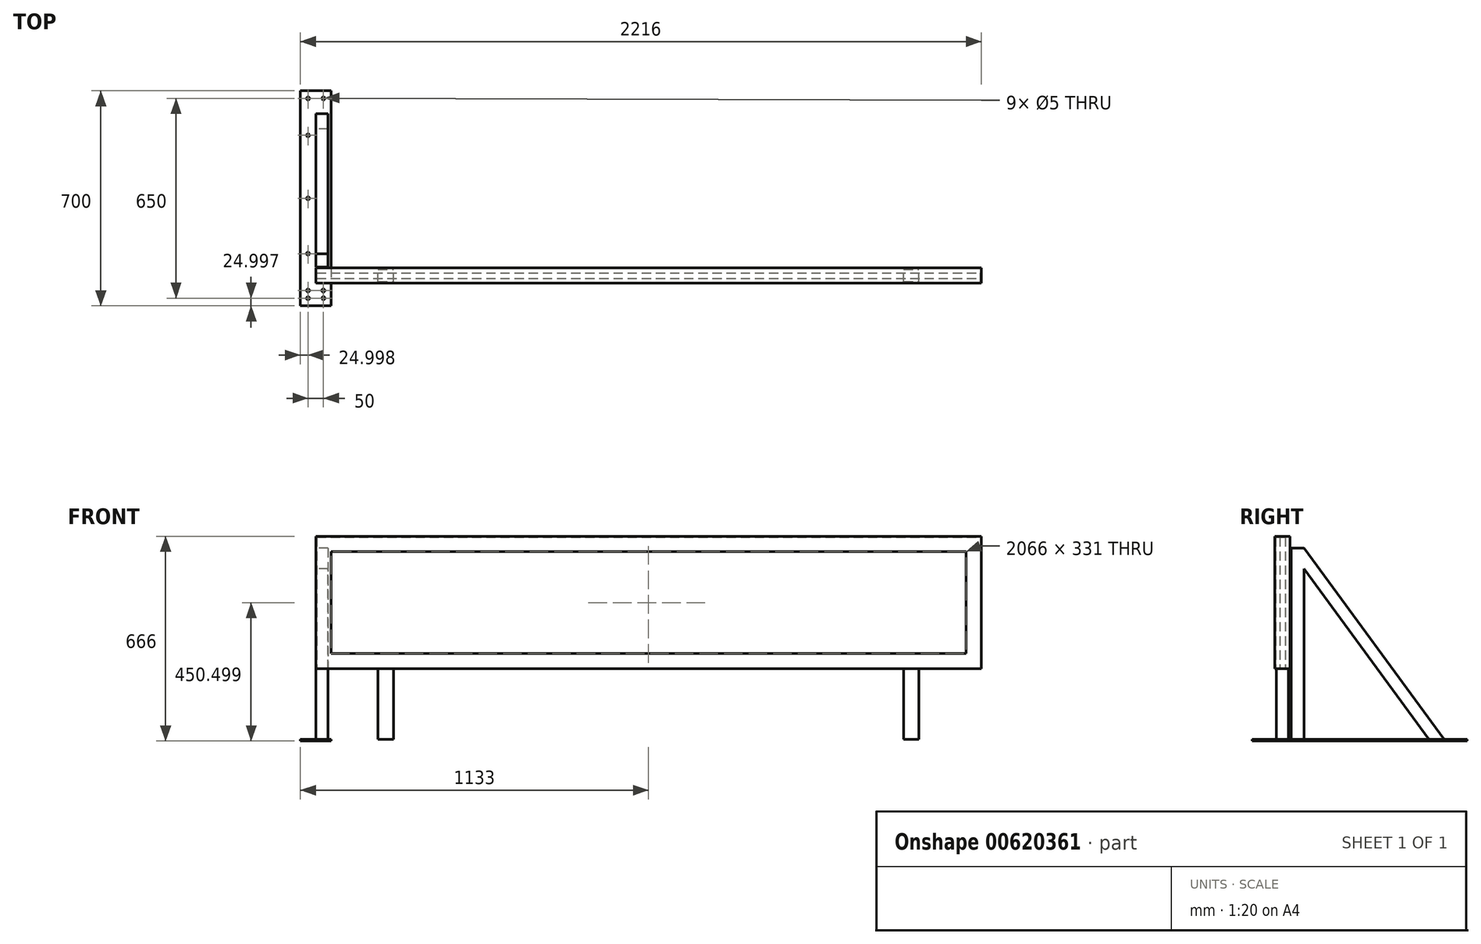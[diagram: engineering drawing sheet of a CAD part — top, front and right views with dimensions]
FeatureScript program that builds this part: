
annotation { "Feature Type Name" : "Feature", "Feature Type Description" : "" }
export const myFeature = defineFeature(function(context is Context, id is Id, definition is map)
    precondition{}
    {
        {
            var Q0;
            Q0=qCreatedBy(makeId("Front.planeOp"),FACE);
            var sketch = newSketch(context, id + "F0", { "sketchPlane" : qUnion([Q0])});
            skLineSegment(sketch, "E0.bottom", {"start": v(-2092.6, 413.56) * mm, "end": v(67.4, 413.56) * mm});
            skLineSegment(sketch, "E0.top", {"start": v(-2092.6, -11.44) * mm, "end": v(67.4, -11.44) * mm});
            skLineSegment(sketch, "E0.left", {"start": v(-2092.6, 413.56) * mm, "end": v(-2092.6, -11.44) * mm});
            skLineSegment(sketch, "E0.right", {"start": v(67.4, 413.56) * mm, "end": v(67.4, -11.44) * mm});
            skLineSegment(sketch, "E1.0", {"start": v(-2042.6, 363.56) * mm, "end": v(17.4, 363.56) * mm});
            skLineSegment(sketch, "E1.1", {"start": v(-2042.6, 363.56) * mm, "end": v(-2042.6, 38.56) * mm});
            skLineSegment(sketch, "E1.2", {"start": v(-2042.6, 38.56) * mm, "end": v(17.4, 38.56) * mm});
            skLineSegment(sketch, "E1.3", {"start": v(17.4, 363.56) * mm, "end": v(17.4, 38.56) * mm});
            skLineSegment(sketch, "E2.bottom", {"start": v(-1892.6, -11.44) * mm, "end": v(-1842.6, -11.44) * mm});
            skLineSegment(sketch, "E2.top", {"start": v(-1892.6, -244.44) * mm, "end": v(-1842.6, -244.44) * mm});
            skLineSegment(sketch, "E2.left", {"start": v(-1892.6, -14.44) * mm, "end": v(-1892.6, -244.44) * mm});
            skLineSegment(sketch, "E2.right", {"start": v(-1842.6, -14.44) * mm, "end": v(-1842.6, -244.44) * mm});
            skLineSegment(sketch, "E3.bottom", {"start": v(-182.6, -11.44) * mm, "end": v(-132.6, -11.44) * mm});
            skLineSegment(sketch, "E3.top", {"start": v(-182.6, -244.44) * mm, "end": v(-132.6, -244.44) * mm});
            skLineSegment(sketch, "E3.left", {"start": v(-182.6, -14.44) * mm, "end": v(-182.6, -244.44) * mm});
            skLineSegment(sketch, "E3.right", {"start": v(-132.6, -14.44) * mm, "end": v(-132.6, -244.44) * mm});
            skLineSegment(sketch, "E4.0", {"start": v(-2095.6, 416.56) * mm, "end": v(70.4, 416.56) * mm});
            skLineSegment(sketch, "E4.1", {"start": v(-2095.6, 416.56) * mm, "end": v(-2095.6, -14.44) * mm});
            skLineSegment(sketch, "E4.2", {"start": v(-2095.6, -14.44) * mm, "end": v(70.4, -14.44) * mm});
            skLineSegment(sketch, "E4.3", {"start": v(70.4, 416.56) * mm, "end": v(70.4, -14.44) * mm});
            skSolve(sketch);
        }
        {
            var Q0;
            Q0=makeQuery(id+"F0.imprint","IMPRINT",FACE,{"disambiguationData":[TD([[makeQuery(id+"F0.imprint","IMPRINT",EDGE,{"derivedFrom":sQuery(id+"F0.wireOp",EDGE,"E1.0")}),-1.0]])]});
            var Q1;
            Q1=makeQuery(id+"F0.imprint","IMPRINT",FACE,{"disambiguationData":[TD([[makeQuery(id+"F0.imprint","IMPRINT",EDGE,{"derivedFrom":sQuery(id+"F0.wireOp",EDGE,"E0.bottom")}),-1.0]])]});
            extrude(context, id + "F1", {"entities" : qUnion([Q0, Q1]), "endBound" : BoundingType.SYMMETRIC, "depth" : 18 * mm, "offsetDistance" : 25 * mm});
        }
        {
            var Q0;
            Q0=makeQuery(id+"F0.imprint","IMPRINT",FACE,{"disambiguationData":[TD([[makeQuery(id+"F0.imprint","IMPRINT",EDGE,{"derivedFrom":sQuery(id+"F0.wireOp",EDGE,"E0.bottom")}),1.0]])]});
            extrude(context, id + "F2", {"entities" : qUnion([Q0]), "endBound" : BoundingType.SYMMETRIC, "depth" : 50 * mm, "offsetDistance" : 25 * mm});
        }
        {
            var Q0;
            Q0=makeQuery(id+"F0.imprint","IMPRINT",FACE,{"disambiguationData":[TD([[makeQuery(id+"F0.imprint","IMPRINT",EDGE,{"derivedFrom":sQuery(id+"F0.wireOp",EDGE,"E2.top")}),1.0]])]});
            var Q1;
            Q1=makeQuery(id+"F0.imprint","IMPRINT",FACE,{"disambiguationData":[TD([[makeQuery(id+"F0.imprint","IMPRINT",EDGE,{"derivedFrom":sQuery(id+"F0.wireOp",EDGE,"E3.top")}),1.0]])]});
            extrude(context, id + "F3", {"entities" : qUnion([Q0, Q1]), "endBound" : BoundingType.SYMMETRIC, "depth" : 40 * mm, "offsetDistance" : 25 * mm});
        }
        {
            var Q0;
            Q0=makeQuery(id+"F2.opExtrude","CAP_FACE",FACE,{"disambiguationData":[OSD([sQuery(id+"F0.wireOp",EDGE,"E0.bottom"),sQuery(id+"F0.wireOp",EDGE,"E0.top"),sQuery(id+"F0.wireOp",EDGE,"E0.left"),sQuery(id+"F0.wireOp",EDGE,"E0.right"),sQuery(id+"F0.wireOp",EDGE,"E2.bottom"),sQuery(id+"F0.wireOp",EDGE,"E3.bottom"),sQuery(id+"F0.wireOp",EDGE,"E4.0"),sQuery(id+"F0.wireOp",EDGE,"E4.1"),sQuery(id+"F0.wireOp",EDGE,"E4.2"),sQuery(id+"F0.wireOp",EDGE,"E4.3")])],"isStart":false});
            var sketch = newSketch(context, id + "F4", { "sketchPlane" : qUnion([Q0])});
            skLineSegment(sketch, "E5.bottom", {"start": v(-2092.6, -11.44) * mm, "end": v(67.4, -11.44) * mm});
            skLineSegment(sketch, "E5.top", {"start": v(-2092.6, 413.56) * mm, "end": v(67.4, 413.56) * mm});
            skLineSegment(sketch, "E5.left", {"start": v(-2092.6, -11.44) * mm, "end": v(-2092.6, 413.56) * mm});
            skLineSegment(sketch, "E5.right", {"start": v(67.4, -11.44) * mm, "end": v(67.4, 413.56) * mm});
            skLineSegment(sketch, "E6.0", {"start": v(-2045.6, 35.56) * mm, "end": v(-2045.6, 366.56) * mm});
            skLineSegment(sketch, "E6.1", {"start": v(-2045.6, 35.56) * mm, "end": v(20.4, 35.56) * mm});
            skLineSegment(sketch, "E6.2", {"start": v(20.4, 35.56) * mm, "end": v(20.4, 366.56) * mm});
            skLineSegment(sketch, "E6.3", {"start": v(-2045.6, 366.56) * mm, "end": v(20.4, 366.56) * mm});
            skSolve(sketch);
        }
        {
            var Q0;
            Q0=makeQuery(id+"F4.imprint","IMPRINT",FACE,{"disambiguationData":[TD([[makeQuery(id+"F4.imprint","IMPRINT",EDGE,{"derivedFrom":sQuery(id+"F4.wireOp",EDGE,"E5.bottom")}),1.0]])]});
            extrude(context, id + "F5", {"entities" : qUnion([Q0]), "operationType" : NewBodyOperationType.ADD, "oppositeDirection" : true, "depth" : 3 * mm, "offsetDistance" : 25 * mm});
        }
        {
            var Q0;
            Q0=makeQuery(id+"F2.opExtrude","SWEPT_FACE",FACE,{"disambiguationData":[OSD([sQuery(id+"F0.wireOp",EDGE,"E4.1")])]});
            var sketch = newSketch(context, id + "F6", { "sketchPlane" : qUnion([Q0])});
            skLineSegment(sketch, "E7", {"start": v(-70.43, 310.78) * mm, "end": v(-70.43, 378.51) * mm});
            skLineSegment(sketch, "E8", {"start": v(-70.43, 378.51) * mm, "end": v(-526.28, -244.44) * mm});
            skLineSegment(sketch, "E9", {"start": v(-526.28, -244.44) * mm, "end": v(-476.71, -244.44) * mm});
            skLineSegment(sketch, "E10", {"start": v(-476.71, -244.44) * mm, "end": v(-70.43, 310.78) * mm});
            skLineSegment(sketch, "E11.bottom", {"start": v(-70.43, 378.51) * mm, "end": v(-28.18, 378.51) * mm});
            skLineSegment(sketch, "E11.top", {"start": v(-70.43, -244.44) * mm, "end": v(-28.18, -244.44) * mm});
            skLineSegment(sketch, "E11.left", {"start": v(-70.43, 378.51) * mm, "end": v(-70.43, -244.44) * mm});
            skLineSegment(sketch, "E11.right", {"start": v(-28.18, 378.51) * mm, "end": v(-28.18, -244.44) * mm});
            skLineSegment(sketch, "E12.bottom", {"start": v(-601.35, -244.44) * mm, "end": v(98.65, -244.44) * mm});
            skLineSegment(sketch, "E12.top", {"start": v(-601.35, -249.44) * mm, "end": v(98.65, -249.44) * mm});
            skLineSegment(sketch, "E12.left", {"start": v(-601.35, -244.44) * mm, "end": v(-601.35, -249.44) * mm});
            skLineSegment(sketch, "E12.right", {"start": v(98.65, -244.44) * mm, "end": v(98.65, -249.44) * mm});
            skSolve(sketch);
        }
        {
            var Q0;
            {var subQ0=sQuery(id+"F6.wireOp",EDGE,"E8");Q0=makeQuery(id+"F6.imprint","IMPRINT",FACE,{"disambiguationData":[TD([[makeQuery(id+"F6.imprint","IMPRINT",EDGE,{"derivedFrom":subQ0}),1.0]])]});}
            var Q1;
            {var subQ5=sQuery(id+"F6.wireOp",EDGE,"E11.bottom");Q1=makeQuery(id+"F6.imprint","IMPRINT",FACE,{"disambiguationData":[TD([[makeQuery(id+"F6.imprint","IMPRINT",EDGE,{"derivedFrom":subQ5}),-1.0]])]});}
            extrude(context, id + "F7", {"entities" : qUnion([Q0, Q1]), "oppositeDirection" : true, "depth" : 40 * mm, "offsetDistance" : 25 * mm});
        }
        {
            var Q0;
            Q0=makeQuery(id+"F6.imprint","IMPRINT",FACE,{"disambiguationData":[TD([[makeQuery(id+"F6.imprint","IMPRINT",EDGE,{"derivedFrom":sQuery(id+"F6.wireOp",EDGE,"E12.top")}),1.0]])]});
            extrude(context, id + "F8", {"entities" : qUnion([Q0]), "endBound" : BoundingType.SYMMETRIC, "depth" : 100 * mm, "offsetDistance" : 25 * mm});
        }
        {
            var Q0;
            Q0=makeQuery(id+"F8.opExtrude","SWEPT_FACE",FACE,{"disambiguationData":[OSD([sQuery(id+"F6.wireOp",EDGE,"E12.bottom")])]});
            var sketch = newSketch(context, id + "F9", { "sketchPlane" : qUnion([Q0])});
            skPoint(sketch, "E13", {"position": v(-2120.6, -73.65) * mm});
            skPoint(sketch, "E14", {"position": v(-2070.6, -73.65) * mm});
            skPoint(sketch, "E15", {"position": v(-2120.6, 71.35) * mm});
            skPoint(sketch, "E16", {"position": v(-2120.6, 251.35) * mm});
            skPoint(sketch, "E17", {"position": v(-2120.6, 456.35) * mm});
            skPoint(sketch, "E18", {"position": v(-2120.6, 576.35) * mm});
            skPoint(sketch, "E19", {"position": v(-2070.6, 576.35) * mm});
            skPoint(sketch, "E20", {"position": v(-2070.97, -48.65) * mm});
            skPoint(sketch, "E21", {"position": v(-2120.6, -48.65) * mm});
            skSolve(sketch);
        }
        {
            var Q0;
            Q0=sQuery(id+"F9.wireOp",VERTEX,"E14");
            var Q1;
            Q1=sQuery(id+"F9.wireOp",VERTEX,"E13");
            var Q2;
            Q2=sQuery(id+"F9.wireOp",VERTEX,"E21");
            var Q3;
            Q3=sQuery(id+"F9.wireOp",VERTEX,"E20");
            var Q4;
            Q4=sQuery(id+"F9.wireOp",VERTEX,"E15");
            var Q5;
            Q5=sQuery(id+"F9.wireOp",VERTEX,"E16");
            var Q6;
            Q6=sQuery(id+"F9.wireOp",VERTEX,"E17");
            var Q7;
            Q7=sQuery(id+"F9.wireOp",VERTEX,"E19");
            var Q8;
            Q8=sQuery(id+"F9.wireOp",VERTEX,"E18");
            var Q9;
            Q9=makeQuery(id+"F8.opExtrude","SWEPT_BODY",BODY,{"disambiguationData":[OSD([sQuery(id+"F6.wireOp",EDGE,"E12.bottom"),sQuery(id+"F6.wireOp",EDGE,"E12.top"),sQuery(id+"F6.wireOp",EDGE,"E12.left"),sQuery(id+"F6.wireOp",EDGE,"E12.right")])]});
            hole(context, id + "F10", {"style" : HoleStyle.C_SINK, "endStyle" : HoleEndStyle.THROUGH, "holeDiameter" : 5 * mm, "cSinkDiameter" : 10 * mm, "cSinkAngle" : 90 * degree, "majorDiameter" : 5 * mm, "isTappedThrough" : true, "tappedDepth" : 12 * mm, "tapClearance" : 3, "locations" : qUnion([Q0, Q1, Q2, Q3, Q4, Q5, Q6, Q7, Q8]), "scope" : qUnion([Q9])});
        }
    });
